# Revit family: Haworth_Worksurface_FlipTopUnit
name_source: partatom
category: Furniture Systems
revit_build: Autodesk Revit 2018 (Build: 20170223_1515(x64)
units: mm (PartAtom-declared; Revit-internal decimal feet)

## family parameters
Always vertical = Yes
Cut with Voids When Loaded = No
OmniClass Number = 23.40.70.14.64.21
OmniClass Title = Systems Furniture
Part Type = Normal
Room Calculation Point = No
Round Connector Dimension = Use Diameter
Shared = No
Work Plane-Based = Yes

## types (4) — shared parameters
Assembly Code = E2020200
Default Elevation = 48"
Description = Haworth - Worksurface - Flip Top Unit
Flip Top Finish = Haworth _ Paint _ Metallic Champagne
Manufacturer = Haworth
Model = Haworth - Worksurface - Flip Top Unit
Revision Number = 3
Size = Verify Final Dim. w/ Haworth
Sustainability Info = http://www.haworth.com
URL = www.haworth.com
URL - Product = www.haworth.com/products/tables/training/planes
Warranty = http://www.haworth.com

## per-type parameters (varying)
| type | Actual Depth | Actual Width |
| Single Sided | 4 3/8" | 8 5/16" |
| Single Sided Wide | 4 3/8" | 11 1/4" |
| Double Sided | 8" | 8 5/16" |
| Double Sided Wide | 8" | 11 1/4" |

type visibility flags: 4 boolean params named "<type name>" — each type sets only its own to Yes (folded from table)

## geometry (parser evidence)
native form markers: Sweep x3
no freeform markers — native parametric forms only
